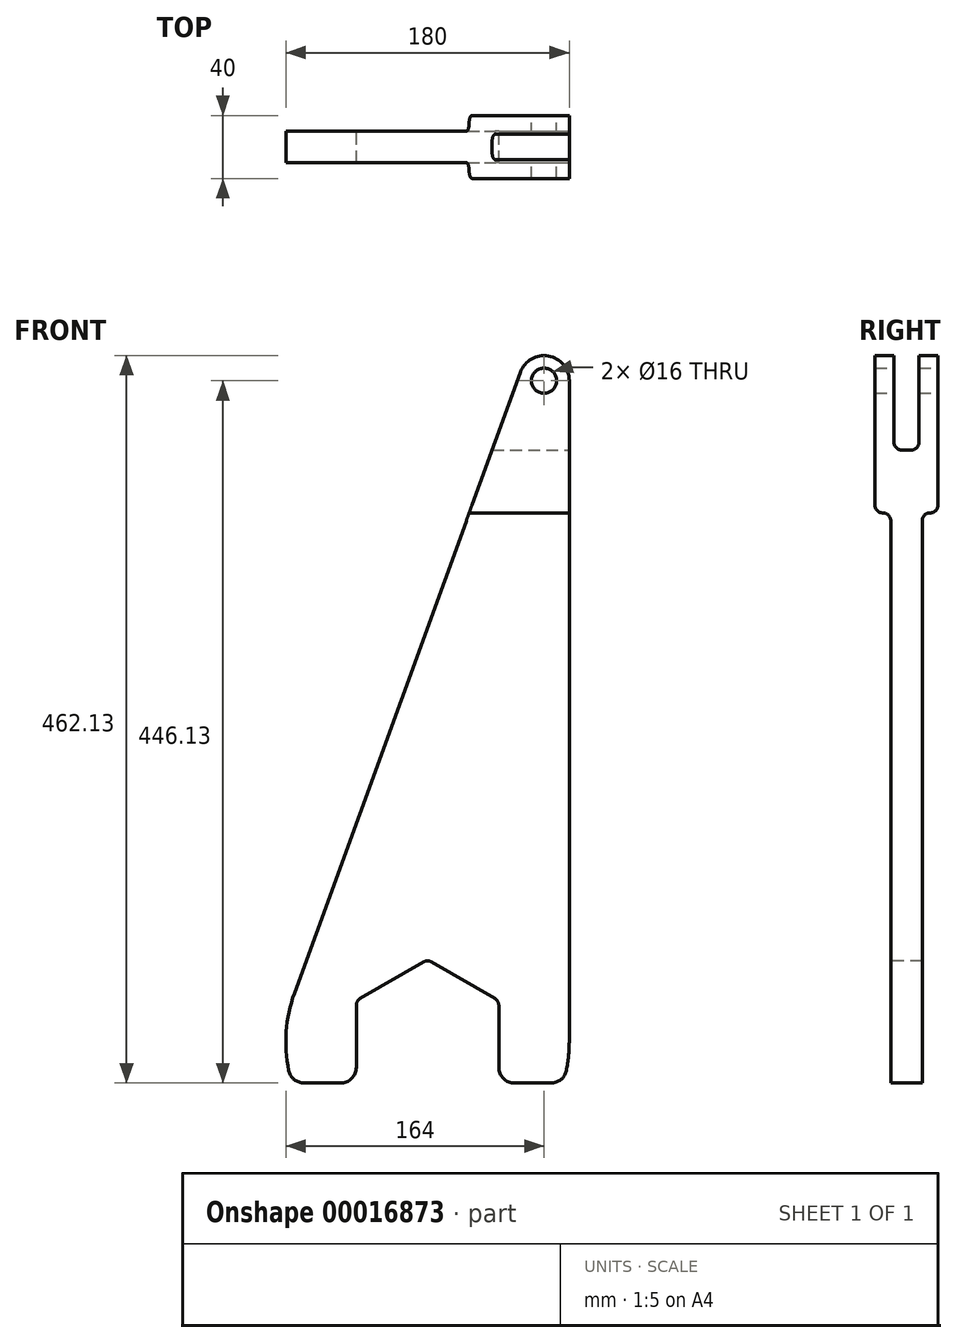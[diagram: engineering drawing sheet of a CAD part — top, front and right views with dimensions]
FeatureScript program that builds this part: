
annotation { "Feature Type Name" : "Feature", "Feature Type Description" : "" }
export const myFeature = defineFeature(function(context is Context, id is Id, definition is map)
    precondition{}
    {
        {
            var Q0;
            Q0=qCreatedBy(makeId("Front.planeOp"),FACE);
            var sketch = newSketch(context, id + "F0", { "sketchPlane" : qUnion([Q0])});
            skCircle(sketch, "E0.cCircle", {"center": v(0, 0) * mm, "radius": 45.25 * mm, "construction": true});
            skLineSegment(sketch, "E0.0", {"start": v(-45.25, -26.13) * mm, "end": v(-45.25, 26.13) * mm});
            skLineSegment(sketch, "E0.1", {"start": v(-45.25, 26.13) * mm, "end": v(0, 52.25) * mm});
            skLineSegment(sketch, "E0.2", {"start": v(0, 52.25) * mm, "end": v(45.25, 26.13) * mm});
            skLineSegment(sketch, "E0.3", {"start": v(45.25, 26.13) * mm, "end": v(45.25, -26.13) * mm});
            skPoint(sketch, "E0.0.midPoint", {"position": v(-45.25, 0) * mm});
            skLineSegment(sketch, "E1", {"start": v(0, 0) * mm, "end": v(119, 0) * mm, "construction": true});
            skLineSegment(sketch, "E2.0", {"start": v(-36, 420) * mm, "end": v(74, 420) * mm, "construction": true});
            skCircle(sketch, "E3", {"center": v(74, 420) * mm, "radius": 8 * mm});
            skArc(sketch, "E4", {"start": v(90, 420) * mm, "mid": v(76.78, 435.76) * mm, "end": v(58.96, 425.47) * mm});
            skArc(sketch, "E5", {"start": v(86.12, -26.13) * mm, "mid": v(89.03, -13.2) * mm, "end": v(90, 0) * mm});
            skLineSegment(sketch, "E6", {"start": v(-86.12, -26.13) * mm, "end": v(-45.25, -26.13) * mm});
            skLineSegment(sketch, "E7.trimOffspring", {"start": v(45.25, -26.13) * mm, "end": v(86.12, -26.13) * mm});
            skPoint(sketch, "E8.orphan", {"position": v(-165, -26.13) * mm});
            skLineSegment(sketch, "E9", {"start": v(58.96, 425.47) * mm, "end": v(-84.58, 30.76) * mm});
            skLineSegment(sketch, "E10", {"start": v(90, 420) * mm, "end": v(90, 0) * mm});
            skArc(sketch, "E11.trimOffspring", {"start": v(-84.58, 30.76) * mm, "mid": v(-89.97, 2.44) * mm, "end": v(-86.12, -26.13) * mm});
            skSolve(sketch);
        }
        {
            var Q0;
            Q0 = qSketchRegion(id + "F0", true);
            extrude(context, id + "F1", {"entities" : qUnion([Q0]), "endBound" : BoundingType.SYMMETRIC, "depth" : 40 * mm});
        }
        {
            var Q0;
            Q0=makeQuery(id+"F1.opExtrude","SWEPT_FACE",FACE,{"disambiguationData":[OSD([sQuery(id+"F0.wireOp",EDGE,"E10")])]});
            var sketch = newSketch(context, id + "F2", { "sketchPlane" : qUnion([Q0])});
            skLineSegment(sketch, "E12", {"start": v(0, 463.36) * mm, "end": v(0, -62.5) * mm, "construction": true});
            skLineSegment(sketch, "E13", {"start": v(-20, 436) * mm, "end": v(20, 436) * mm});
            skLineSegment(sketch, "E14.0", {"start": v(-20, 336) * mm, "end": v(-10, 336) * mm});
            skLineSegment(sketch, "E15.0", {"start": v(-10, 463.36) * mm, "end": v(-10, 436) * mm});
            skLineSegment(sketch, "E16", {"start": v(-10, -62.5) * mm, "end": v(-86.65, -62.5) * mm});
            skLineSegment(sketch, "E17", {"start": v(-86.65, -62.5) * mm, "end": v(-86.65, 336) * mm});
            skLineSegment(sketch, "E18", {"start": v(-86.65, 336) * mm, "end": v(-20, 336) * mm});
            skLineSegment(sketch, "E19.trimOffspring", {"start": v(-10, 336) * mm, "end": v(-10, -62.5) * mm});
            skLineSegment(sketch, "E20.MirrorCS", {"start": v(20, 336) * mm, "end": v(10, 336) * mm});
            skLineSegment(sketch, "E21.MirrorCS", {"start": v(86.65, 336) * mm, "end": v(20, 336) * mm});
            skLineSegment(sketch, "E22.MirrorCS", {"start": v(10, 336) * mm, "end": v(10, -62.5) * mm});
            skLineSegment(sketch, "E23.MirrorCS", {"start": v(10, -62.5) * mm, "end": v(86.65, -62.5) * mm});
            skLineSegment(sketch, "E24.MirrorCS", {"start": v(86.65, -62.5) * mm, "end": v(86.65, 336) * mm});
            skSolve(sketch);
        }
        {
            var Q0;
            Q0 = qSketchRegion(id + "F2", true);
            extrude(context, id + "F3", {"entities" : qUnion([Q0]), "operationType" : NewBodyOperationType.REMOVE, "endBound" : BoundingType.THROUGH_ALL, "oppositeDirection" : true, "depth" : 25 * mm});
        }
        {
            var Q0;
            Q0=makeQuery(id+"F1.opExtrude","SWEPT_FACE",FACE,{"disambiguationData":[OSD([sQuery(id+"F0.wireOp",EDGE,"E10")])]});
            var sketch = newSketch(context, id + "F4", { "sketchPlane" : qUnion([Q0])});
            skLineSegment(sketch, "E25", {"start": v(0, 472.38) * mm, "end": v(0, 336) * mm, "construction": true});
            skLineSegment(sketch, "E26", {"start": v(-20, 436) * mm, "end": v(20, 436) * mm, "construction": true});
            skLineSegment(sketch, "E27.0", {"start": v(-8, 472.38) * mm, "end": v(-8, 336) * mm, "construction": true});
            skLineSegment(sketch, "E28.MirrorCS", {"start": v(8, 472.38) * mm, "end": v(8, 336) * mm, "construction": true});
            skLineSegment(sketch, "E29.0", {"start": v(-20, 376) * mm, "end": v(20, 376) * mm, "construction": true});
            skLineSegment(sketch, "E30.bottom", {"start": v(-8, 472.38) * mm, "end": v(8, 472.38) * mm});
            skLineSegment(sketch, "E30.top", {"start": v(-8, 376) * mm, "end": v(8, 376) * mm});
            skLineSegment(sketch, "E30.left", {"start": v(-8, 472.38) * mm, "end": v(-8, 376) * mm});
            skLineSegment(sketch, "E30.right", {"start": v(8, 472.38) * mm, "end": v(8, 376) * mm});
            skSolve(sketch);
        }
        {
            var Q0;
            Q0 = qSketchRegion(id + "F4", true);
            extrude(context, id + "F5", {"entities" : qUnion([Q0]), "operationType" : NewBodyOperationType.REMOVE, "endBound" : BoundingType.THROUGH_ALL, "oppositeDirection" : true, "depth" : 25 * mm});
        }
        {
            var Q0;
            Q0=makeQuery(id+"F5.boolean.opBoolean","COPY",EDGE,{"derivedFrom":makeQuery(id+"F5.opExtrude","SWEPT_EDGE",EDGE,{"disambiguationData":[OSD([sQuery(id+"F4.wireOp",EDGE,"E30.top"),sQuery(id+"F4.wireOp",EDGE,"E30.left")])]})});
            var Q1;
            Q1=makeQuery(id+"F5.boolean.opBoolean","COPY",EDGE,{"derivedFrom":makeQuery(id+"F5.opExtrude","SWEPT_EDGE",EDGE,{"disambiguationData":[OSD([sQuery(id+"F4.wireOp",EDGE,"E30.top"),sQuery(id+"F4.wireOp",EDGE,"E30.right")])]})});
            var Q2;
            Q2=makeQuery(id+"F3.boolean.opBoolean","INTERSECT",EDGE,{"derivedFrom":[makeQuery(id+"F1.opExtrude","CAP_FACE",FACE,{"disambiguationData":[OSD([sQuery(id+"F0.wireOp",EDGE,"E0.0"),sQuery(id+"F0.wireOp",EDGE,"E0.1"),sQuery(id+"F0.wireOp",EDGE,"E0.2"),sQuery(id+"F0.wireOp",EDGE,"E0.3"),sQuery(id+"F0.wireOp",EDGE,"E3"),sQuery(id+"F0.wireOp",EDGE,"E4"),sQuery(id+"F0.wireOp",EDGE,"E5"),sQuery(id+"F0.wireOp",EDGE,"E6"),sQuery(id+"F0.wireOp",EDGE,"E7.trimOffspring"),sQuery(id+"F0.wireOp",EDGE,"E9"),sQuery(id+"F0.wireOp",EDGE,"E10"),sQuery(id+"F0.wireOp",EDGE,"E11.trimOffspring")])],"isStart":true}),makeQuery(id+"F3.opExtrude","SWEPT_FACE",FACE,{"disambiguationData":[OSD([sQuery(id+"F2.wireOp",EDGE,"E20.MirrorCS"),sQuery(id+"F2.wireOp",EDGE,"E21.MirrorCS")])]})]});
            var Q3;
            Q3=makeQuery(id+"F3.boolean.opBoolean","COPY",EDGE,{"derivedFrom":makeQuery(id+"F3.opExtrude","SWEPT_EDGE",EDGE,{"disambiguationData":[OSD([sQuery(id+"F2.wireOp",EDGE,"E20.MirrorCS"),sQuery(id+"F2.wireOp",EDGE,"E22.MirrorCS")])]})});
            var Q4;
            Q4=makeQuery(id+"F3.boolean.opBoolean","COPY",EDGE,{"derivedFrom":makeQuery(id+"F3.opExtrude","SWEPT_EDGE",EDGE,{"disambiguationData":[OSD([sQuery(id+"F2.wireOp",EDGE,"E14.0"),sQuery(id+"F2.wireOp",EDGE,"E19.trimOffspring")])]})});
            var Q5;
            Q5=makeQuery(id+"F3.boolean.opBoolean","INTERSECT",EDGE,{"derivedFrom":[makeQuery(id+"F1.opExtrude","CAP_FACE",FACE,{"disambiguationData":[OSD([sQuery(id+"F0.wireOp",EDGE,"E0.0"),sQuery(id+"F0.wireOp",EDGE,"E0.1"),sQuery(id+"F0.wireOp",EDGE,"E0.2"),sQuery(id+"F0.wireOp",EDGE,"E0.3"),sQuery(id+"F0.wireOp",EDGE,"E3"),sQuery(id+"F0.wireOp",EDGE,"E4"),sQuery(id+"F0.wireOp",EDGE,"E5"),sQuery(id+"F0.wireOp",EDGE,"E6"),sQuery(id+"F0.wireOp",EDGE,"E7.trimOffspring"),sQuery(id+"F0.wireOp",EDGE,"E9"),sQuery(id+"F0.wireOp",EDGE,"E10"),sQuery(id+"F0.wireOp",EDGE,"E11.trimOffspring")])],"isStart":false}),makeQuery(id+"F3.opExtrude","SWEPT_FACE",FACE,{"disambiguationData":[OSD([sQuery(id+"F2.wireOp",EDGE,"E14.0"),sQuery(id+"F2.wireOp",EDGE,"E18")])]})]});
            fillet(context, id + "F6", {"entities" : qUnion([Q0, Q1, Q2, Q3, Q4, Q5]), "radius" : 5 * mm, "tangentPropagation" : true, "allowEdgeOverflow" : false});
        }
        {
            var Q0;
            Q0=makeQuery(id+"F1.opExtrude","SWEPT_EDGE",EDGE,{"disambiguationData":[OSD([sQuery(id+"F0.wireOp",EDGE,"E0.0"),sQuery(id+"F0.wireOp",EDGE,"E0.1")])]});
            var Q1;
            Q1=makeQuery(id+"F1.opExtrude","SWEPT_EDGE",EDGE,{"disambiguationData":[OSD([sQuery(id+"F0.wireOp",EDGE,"E0.1"),sQuery(id+"F0.wireOp",EDGE,"E0.2")])]});
            var Q2;
            Q2=makeQuery(id+"F1.opExtrude","SWEPT_EDGE",EDGE,{"disambiguationData":[OSD([sQuery(id+"F0.wireOp",EDGE,"E0.2"),sQuery(id+"F0.wireOp",EDGE,"E0.3")])]});
            fillet(context, id + "F7", {"entities" : qUnion([Q0, Q1, Q2]), "radius" : 5 * mm, "tangentPropagation" : true, "allowEdgeOverflow" : false});
        }
        {
            var Q0;
            Q0=makeQuery(id+"F1.opExtrude","SWEPT_EDGE",EDGE,{"disambiguationData":[OSD([sQuery(id+"F0.wireOp",EDGE,"E0.0"),sQuery(id+"F0.wireOp",EDGE,"E6")])]});
            var Q1;
            Q1=makeQuery(id+"F1.opExtrude","SWEPT_EDGE",EDGE,{"disambiguationData":[OSD([sQuery(id+"F0.wireOp",EDGE,"E6"),sQuery(id+"F0.wireOp",EDGE,"E11.trimOffspring")])]});
            var Q2;
            Q2=makeQuery(id+"F1.opExtrude","SWEPT_EDGE",EDGE,{"disambiguationData":[OSD([sQuery(id+"F0.wireOp",EDGE,"E0.3"),sQuery(id+"F0.wireOp",EDGE,"E7.trimOffspring")])]});
            var Q3;
            Q3=makeQuery(id+"F1.opExtrude","SWEPT_EDGE",EDGE,{"disambiguationData":[OSD([sQuery(id+"F0.wireOp",EDGE,"E5"),sQuery(id+"F0.wireOp",EDGE,"E7.trimOffspring")])]});
            fillet(context, id + "F8", {"entities" : qUnion([Q0, Q1, Q2, Q3]), "radius" : 10 * mm, "tangentPropagation" : true, "allowEdgeOverflow" : false});
        }
    });
